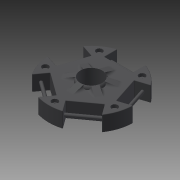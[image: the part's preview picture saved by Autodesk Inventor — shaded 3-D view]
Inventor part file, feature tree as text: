
AUTODESK INVENTOR PART (.ipt)
format: ipt  version: 2014 SP2 (Build 180246200, 246)  size: 1,177,600 bytes
history: native  units: mm
features: extrude x10, sketch x10, fillet x6, projected_geometry x3, pattern_circular x2
ambient origin geometry x8: Origin, YZ Plane, XZ Plane, XY Plane, X Axis, Y Axis, Z Axis, Center Point
bodies: Solid1 (feature_tree)
feature tree (31):
  extrude  "Extrusion1"  Depth=10.0mm TaperAngle=0.0deg
  extrude  "Extrusion2"  Depth=10.0mm TaperAngle=0.0deg
  extrude  "Extrusion3"  Depth=50.0mm TaperAngle=360.0deg
  extrude  "Extrusion4"  Depth=20.0mm TaperAngle=0.0deg
  pattern_circular  "Circular Pattern1"  Count=5 Angle=360.0deg
  extrude  "Extrusion5"  Depth=50.0mm TaperAngle=360.0deg
  extrude  "Extrusion6"  Depth=0.3mm
  extrude  "Extrusion7"  Depth=2.5mm
  fillet  "Fillet1"  Radius=2.5mm
  extrude  "Extrusion8"  Depth=4.0mm TaperAngle=0.0deg
  fillet  "Fillet2"  Radius=5.0mm
  fillet  "Fillet3"  Radius=2.0mm
  extrude  "Extrusion9"  Depth=60.0mm TaperAngle=360.0deg
  extrude  "Extrusion10"  [1 undecoded]
  fillet  "Fillet4"  [1 undecoded]
  fillet  "Fillet5"  [1 undecoded]
  fillet  "Fillet6"  [1 undecoded]
  pattern_circular  "Circular Pattern2"  [2 undecoded]
  sketch  "Sketch1"  dims[d1=10.0mm d2=0.0mm d4=10.0mm d5=0.0mm]
  sketch  "Sketch2"  dims[d10=50.0mm d12=360.0deg d14=10.0mm d15=0.0mm]
  sketch  "Sketch3"  dims[d17=20.0mm d18=0.0mm d19=50.0mm d20=360.0deg]
  sketch  "Sketch4"  dims[d25=50.0mm d27=360.0deg d29=20.0mm d30=0.0mm d32=50.0mm d34=360.0deg]
  projected_geometry  "Projected Loop1"
  sketch  "Sketch5"  dims[d36=2.0mm d37=0.0mm d39=50.0mm d41=360.0deg]
  sketch  "Sketch6"  dims[d43=5.0mm d44=0.0mm d45=0.3mm]
  sketch  "Sketch7"  dims[d47=2.0mm d48=12.0mm d49=0.0mm d50=0.0mm d51=2.5mm d52=2.5mm]
  sketch  "Sketch8"  dims[d53=4.0mm d54=0.0mm d55=4.0mm d56=0.0mm d57=5.0mm d58=2.0mm]
  sketch  "Sketch9"  dims[d59=2.0mm d60=60.0mm d61=360.0deg]
  projected_geometry  "Projected Loop2"
  sketch  "Sketch10"
  projected_geometry  "Projected Loop3"
note: 6 required parameter values undecoded (feature->parameter linkage not recoverable at this tier; creation-order binding heuristic only, values carry confidence <= 0.55)
